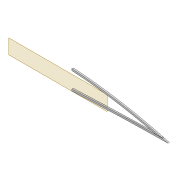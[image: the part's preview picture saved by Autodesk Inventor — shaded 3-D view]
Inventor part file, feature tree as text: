
AUTODESK INVENTOR PART (.ipt)
format: ipt  version: 2022 (Build 260153000, 153)  size: 413,696 bytes
history: native  units: mm
features: extrude x8, sketch x7, projected_geometry x6, fillet x2, shell x1, plane x1
ambient origin geometry x8: Origin, YZ Plane, XZ Plane, XY Plane, X Axis, Y Axis, Z Axis, Center Point
bodies: Solid1 (feature_tree)
feature tree (25):
  extrude  "Extrusion1"  Depth=5.0mm
  shell  "Shell1"  Thickness=2.0mm
  extrude  "Extrusion8"  Depth=5.9mm
  extrude  "Extrusion3"  Depth=10.0mm TaperAngle=0.0deg
  extrude  "Extrusion4"  Depth=2.0mm
  fillet  "Fillet1"  Radius=5.0mm
  sketch  "Sketch10"  dims[d22=4.0mm d23=0.0mm d31=2.0mm d32=5.0mm]
  extrude  "Extrusion5"  Depth=2.5mm
  plane  "Work Plane2"
  extrude  "Extrusion9"  Depth=1.6mm
  fillet  "Fillet2"  Radius=2.5mm
  extrude  "Extrusion10"  Depth=6.0mm
  extrude  "Extrusion11"  Depth=4.0mm TaperAngle=0.0deg
  sketch  "Sketch3"  dims[d0=4.0mm d1=0.0mm d2=5.0mm d7=2.0mm]
  sketch  "Sketch8"  dims[d8=2.0mm d9=5.9mm]
  sketch  "Sketch9"  dims[d13=10.0mm d14=0.0mm d16=10.0mm d17=0.0mm]
  projected_geometry  "Projected Loop4"
  projected_geometry  "Projected Loop10"
  sketch  "Sketch24"  dims[d34=1.6mm d35=2.5mm]
  projected_geometry  "Projected Loop11"
  projected_geometry  "Projected Loop12"
  projected_geometry  "Projected Loop13"
  sketch  "Sketch26"  dims[d37=5.0mm d38=1.6mm d40=2.5mm]
  projected_geometry  "Projected Loop14"
  sketch  "Sketch27"  dims[d62=80.0mm d63=6.0mm d64=4.0mm d65=0.0mm d66=3.0mm d67=12.0mm d68=5.0mm d69=17.0mm d70=12.0mm d71=3.05mm d72=10.0mm d73=0.0mm d74=2.0mm d75=100.0mm d77=20.0mm d78=0.5mm d79=10.0mm d80=0.0mm d81=10.0mm d82=0.0mm]
